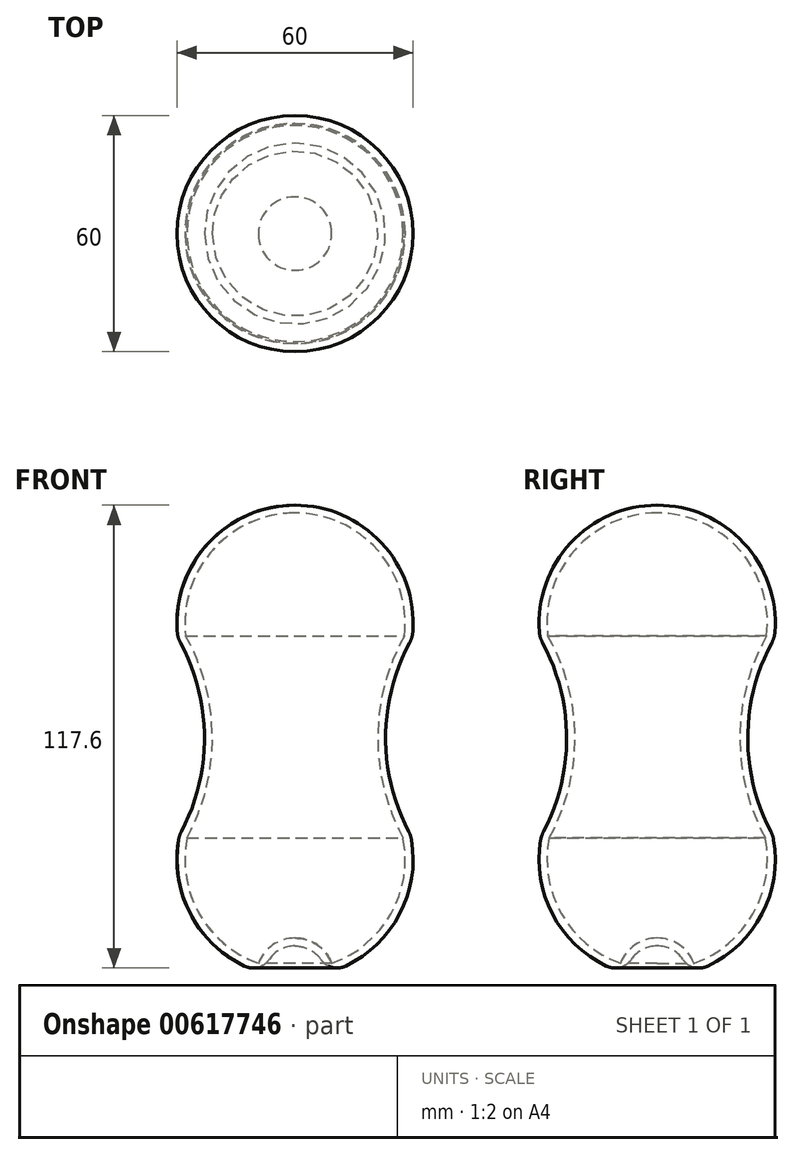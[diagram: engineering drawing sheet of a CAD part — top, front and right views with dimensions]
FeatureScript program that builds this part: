
annotation { "Feature Type Name" : "Feature", "Feature Type Description" : "" }
export const myFeature = defineFeature(function(context is Context, id is Id, definition is map)
    precondition{}
    {
        {
            var Q0;
            Q0=qCreatedBy(makeId("Front.planeOp"),FACE);
            var sketch = newSketch(context, id + "F0", { "sketchPlane" : qUnion([Q0])});
            skLineSegment(sketch, "E0", {"start": v(0, 8) * mm, "end": v(0, 10) * mm});
            skArc(sketch, "E1", {"start": v(0, 120) * mm, "mid": v(-22.52, 109.81) * mm, "end": v(-29.76, 86.18) * mm});
            skArc(sketch, "E2", {"start": v(-29.36, 36.18) * mm, "mid": v(-25.6, 14.37) * mm, "end": v(-7.93, 1.07) * mm});
            skArc(sketch, "E3", {"start": v(-29.36, 36.18) * mm, "mid": v(-23.01, 61.23) * mm, "end": v(-29.76, 86.18) * mm});
            skArc(sketch, "E4", {"start": v(0, 8) * mm, "mid": v(-5.27, 6.02) * mm, "end": v(-7.93, 1.07) * mm});
            skArc(sketch, "E5.0", {"start": v(-27.46, 35.48) * mm, "mid": v(-21.01, 61.2) * mm, "end": v(-27.82, 86.81) * mm});
            skArc(sketch, "E5.1", {"start": v(0, 118) * mm, "mid": v(-20.9, 108.64) * mm, "end": v(-27.82, 86.81) * mm});
            skArc(sketch, "E6.0", {"start": v(-27.46, 35.48) * mm, "mid": v(-24.34, 16.16) * mm, "end": v(-9.33, 3.6) * mm});
            skArc(sketch, "E7.0", {"start": v(0, 10) * mm, "mid": v(-5.66, 8.25) * mm, "end": v(-9.33, 3.6) * mm});
            skLineSegment(sketch, "E8.trimOffspring", {"start": v(0, 118) * mm, "end": v(0, 120) * mm});
            skLineSegment(sketch, "E9", {"start": v(0, 0) * mm, "end": v(0, 150.45) * mm, "construction": true});
            skSolve(sketch);
        }
        {
            var Q0;
            Q0=makeQuery(id+"F0.imprint","IMPRINT",FACE,{"disambiguationData":[TD([[makeQuery(id+"F0.imprint","IMPRINT",EDGE,{"derivedFrom":sQuery(id+"F0.wireOp",EDGE,"E0")}),1.0]])]});
            var Q1;
            Q1=sQuery(id+"F0.wireOp",EDGE,"E9");
            revolve(context, id + "F1", {"entities" : qUnion([Q0]), "axis" : qUnion([Q1]), "revolveType" : RevolveType.FULL});
        }
        {
            var Q0;
            Q0=makeQuery(id+"F1.opRevolve","SWEPT_FACE",FACE,{"disambiguationData":[OSD([sQuery(id+"F0.wireOp",EDGE,"E3")])]});
            fillet(context, id + "F2", {"entities" : qUnion([Q0]), "radius" : 7 * mm, "tangentPropagation" : true, "allowEdgeOverflow" : false});
        }
        {
            var Q0;
            Q0=makeQuery(id+"F1.opRevolve","SWEPT_EDGE",EDGE,{"disambiguationData":[OSD([sQuery(id+"F0.wireOp",EDGE,"E2"),sQuery(id+"F0.wireOp",EDGE,"E4")])]});
            fillet(context, id + "F3", {"entities" : qUnion([Q0]), "radius" : 5 * mm, "tangentPropagation" : true, "allowEdgeOverflow" : false});
        }
    });
